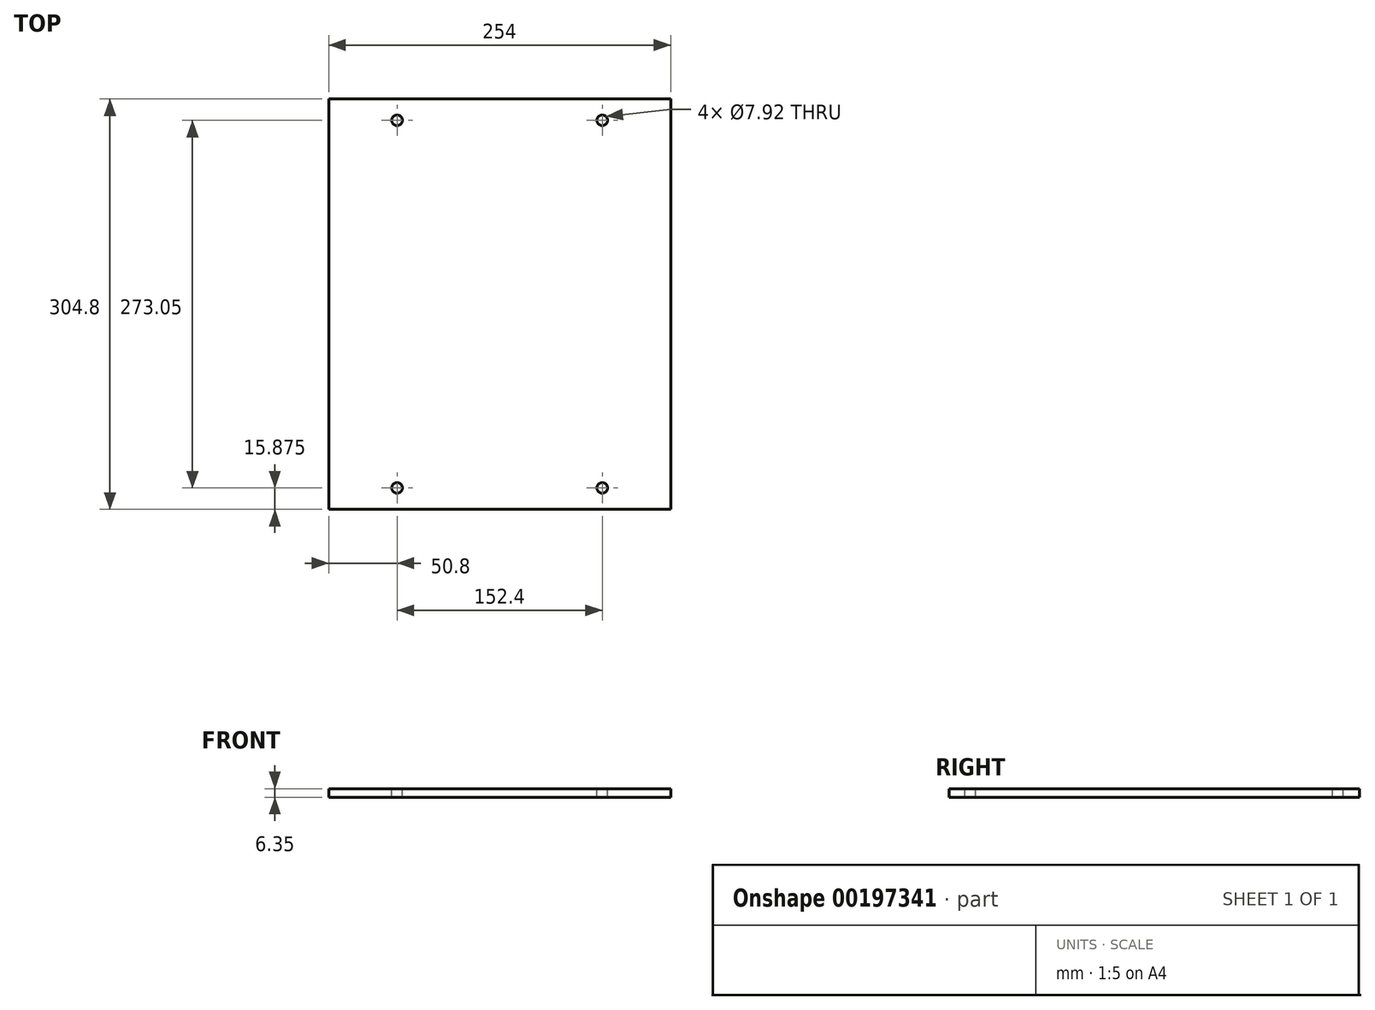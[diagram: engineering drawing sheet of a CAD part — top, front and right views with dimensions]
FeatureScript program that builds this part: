
annotation { "Feature Type Name" : "Feature", "Feature Type Description" : "" }
export const myFeature = defineFeature(function(context is Context, id is Id, definition is map)
    precondition{}
    {
        {
            var Q0;
            Q0=qCreatedBy(makeId("Top.planeOp"),FACE);
            var sketch = newSketch(context, id + "F0", { "sketchPlane" : qUnion([Q0])});
            skLineSegment(sketch, "E0.bottom", {"start": v(0, 0) * mm, "end": v(254, 0) * mm});
            skLineSegment(sketch, "E0.top", {"start": v(0, 304.8) * mm, "end": v(254, 304.8) * mm});
            skLineSegment(sketch, "E0.left", {"start": v(0, 0) * mm, "end": v(0, 304.8) * mm});
            skLineSegment(sketch, "E0.right", {"start": v(254, 0) * mm, "end": v(254, 304.8) * mm});
            skSolve(sketch);
        }
        {
            var Q0;
            Q0=qSketchRegion(id+"F0",true);
            extrude(context, id + "F1", {"entities" : qUnion([Q0]), "oppositeDirection" : true, "depth" : 6.35 * mm});
        }
        {
            var Q0;
            Q0=makeQuery(id+"F1.opExtrude","CAP_FACE",FACE,{"disambiguationData":[OSD([sQuery(id+"F0.wireOp",EDGE,"E0.bottom"),sQuery(id+"F0.wireOp",EDGE,"E0.top"),sQuery(id+"F0.wireOp",EDGE,"E0.left"),sQuery(id+"F0.wireOp",EDGE,"E0.right")])],"isStart":true});
            var sketch = newSketch(context, id + "F2", { "sketchPlane" : qUnion([Q0])});
            skCircle(sketch, "E1", {"center": v(50.8, 288.93) * mm, "radius": 3.96 * mm});
            skCircle(sketch, "E2", {"center": v(203.2, 288.93) * mm, "radius": 3.96 * mm});
            skCircle(sketch, "E3", {"center": v(203.2, 15.88) * mm, "radius": 3.96 * mm});
            skCircle(sketch, "E4", {"center": v(50.8, 15.88) * mm, "radius": 3.96 * mm});
            skSolve(sketch);
        }
        {
            var Q0;
            Q0=sQuery(id+"F2.wireOp",VERTEX,"E1.center");
            var Q1;
            Q1=makeQuery(id+"F1.opExtrude","SWEPT_BODY",BODY,{"disambiguationData":[OSD([sQuery(id+"F0.wireOp",EDGE,"E0.bottom"),sQuery(id+"F0.wireOp",EDGE,"E0.top"),sQuery(id+"F0.wireOp",EDGE,"E0.left"),sQuery(id+"F0.wireOp",EDGE,"E0.right")])]});
            hole(context, id + "F3", {"style" : HoleStyle.SIMPLE, "endStyle" : HoleEndStyle.THROUGH, "holeDiameter" : 7.92 * mm, "locations" : qUnion([Q0]), "scope" : qUnion([Q1]), "isTappedThrough" : true});
        }
        {
            var Q0;
            Q0=sQuery(id+"F2.wireOp",VERTEX,"E2.center");
            var Q1;
            Q1=makeQuery(id+"F1.opExtrude","SWEPT_BODY",BODY,{"disambiguationData":[OSD([sQuery(id+"F0.wireOp",EDGE,"E0.bottom"),sQuery(id+"F0.wireOp",EDGE,"E0.top"),sQuery(id+"F0.wireOp",EDGE,"E0.left"),sQuery(id+"F0.wireOp",EDGE,"E0.right")])]});
            hole(context, id + "F4", {"style" : HoleStyle.SIMPLE, "endStyle" : HoleEndStyle.THROUGH, "holeDiameter" : 7.92 * mm, "locations" : qUnion([Q0]), "scope" : qUnion([Q1]), "isTappedThrough" : true});
        }
        {
            var Q0;
            Q0=sQuery(id+"F2.wireOp",VERTEX,"E3.center");
            var Q1;
            Q1=makeQuery(id+"F1.opExtrude","SWEPT_BODY",BODY,{"disambiguationData":[OSD([sQuery(id+"F0.wireOp",EDGE,"E0.bottom"),sQuery(id+"F0.wireOp",EDGE,"E0.top"),sQuery(id+"F0.wireOp",EDGE,"E0.left"),sQuery(id+"F0.wireOp",EDGE,"E0.right")])]});
            hole(context, id + "F5", {"style" : HoleStyle.SIMPLE, "endStyle" : HoleEndStyle.THROUGH, "holeDiameter" : 7.92 * mm, "locations" : qUnion([Q0]), "scope" : qUnion([Q1]), "isTappedThrough" : true});
        }
        {
            var Q0;
            Q0=sQuery(id+"F2.wireOp",VERTEX,"E4.center");
            var Q1;
            Q1=makeQuery(id+"F1.opExtrude","SWEPT_BODY",BODY,{"disambiguationData":[OSD([sQuery(id+"F0.wireOp",EDGE,"E0.bottom"),sQuery(id+"F0.wireOp",EDGE,"E0.top"),sQuery(id+"F0.wireOp",EDGE,"E0.left"),sQuery(id+"F0.wireOp",EDGE,"E0.right")])]});
            hole(context, id + "F6", {"style" : HoleStyle.SIMPLE, "endStyle" : HoleEndStyle.THROUGH, "holeDiameter" : 7.92 * mm, "locations" : qUnion([Q0]), "scope" : qUnion([Q1]), "isTappedThrough" : true});
        }
    });
